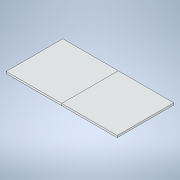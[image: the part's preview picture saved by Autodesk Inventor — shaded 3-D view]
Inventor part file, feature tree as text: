
AUTODESK INVENTOR PART (.ipt)
format: ipt  version: 2021 (Build 250183000, 183)  size: 111,104 bytes
history: imported  units: in
note: dims shown in document units (in); Inventor stores cm internally (conversion verified against a paired STEP export)
features: imported_body x1
ambient origin geometry x8: Origin, YZ Plane, XZ Plane, XY Plane, X Axis, Y Axis, Z Axis, Center Point
bodies: Solid1 (imported_parasolid), Solid2 (imported_parasolid), Body1 (imported_parasolid), Body2 (imported_parasolid)
feature tree (1):
  imported_body  NMx_Import_Brep_tag  [imported B-rep: ~18 faces, bbox_mm=[2000.0, 40.0, 1020.0]]
